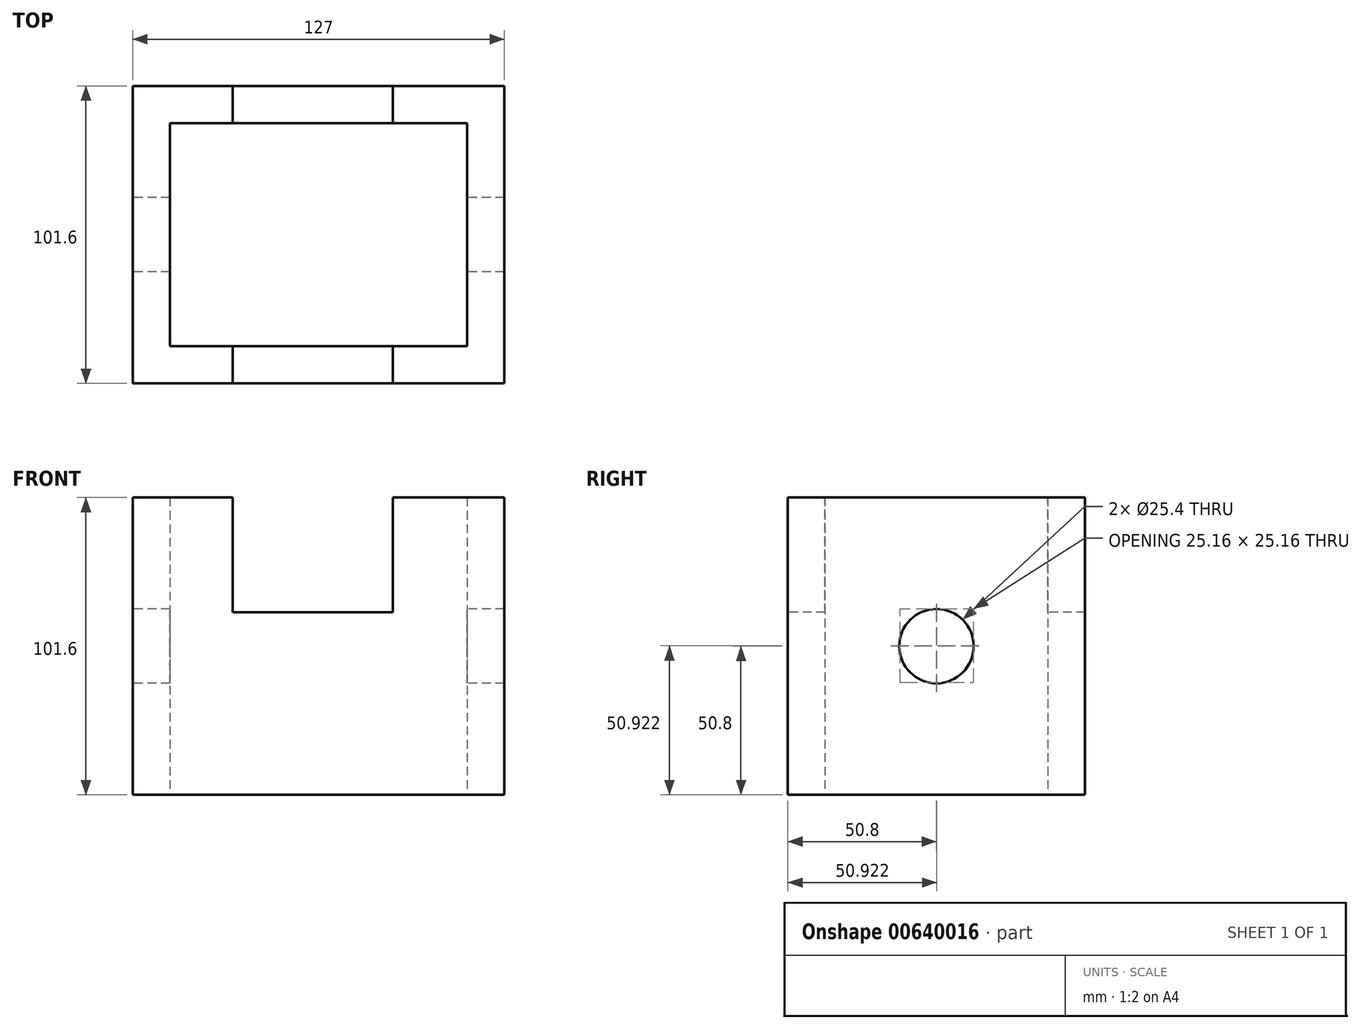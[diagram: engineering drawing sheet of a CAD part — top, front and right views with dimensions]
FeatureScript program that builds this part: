
annotation { "Feature Type Name" : "Feature", "Feature Type Description" : "" }
export const myFeature = defineFeature(function(context is Context, id is Id, definition is map)
    precondition{}
    {
        {
            var Q0;
            Q0=qCreatedBy(makeId("Top.planeOp"),FACE);
            var sketch = newSketch(context, id + "F0", { "sketchPlane" : qUnion([Q0])});
            skLineSegment(sketch, "E0.bottom", {"start": v(92.9, -48.3) * mm, "end": v(-34.1, -48.3) * mm});
            skLineSegment(sketch, "E0.top", {"start": v(92.9, 53.3) * mm, "end": v(-34.1, 53.3) * mm});
            skLineSegment(sketch, "E0.left", {"start": v(92.9, -48.3) * mm, "end": v(92.9, 53.3) * mm});
            skLineSegment(sketch, "E0.right", {"start": v(-34.1, -48.3) * mm, "end": v(-34.1, 53.3) * mm});
            skLineSegment(sketch, "E1.bottom", {"start": v(-21.4, 40.6) * mm, "end": v(80.2, 40.6) * mm});
            skLineSegment(sketch, "E1.top", {"start": v(-21.4, -35.6) * mm, "end": v(80.2, -35.6) * mm});
            skLineSegment(sketch, "E1.left", {"start": v(-21.4, 40.6) * mm, "end": v(-21.4, -35.6) * mm});
            skLineSegment(sketch, "E1.right", {"start": v(80.2, 40.6) * mm, "end": v(80.2, -35.6) * mm});
            skSolve(sketch);
        }
        {
            var Q0;
            Q0=makeQuery(id+"F0.imprint","IMPRINT",FACE,{"disambiguationData":[TD([[makeQuery(id+"F0.imprint","IMPRINT",EDGE,{"derivedFrom":sQuery(id+"F0.wireOp",EDGE,"E0.bottom")}),-1.0]])]});
            extrude(context, id + "F1", {"entities" : qUnion([Q0]), "depth" : 101.6 * mm, "offsetDistance" : 25.4 * mm});
        }
        {
            var Q0;
            Q0=makeQuery(id+"F1.opExtrude","SWEPT_FACE",FACE,{"disambiguationData":[OSD([sQuery(id+"F0.wireOp",EDGE,"E0.bottom")])]});
            var sketch = newSketch(context, id + "F2", { "sketchPlane" : qUnion([Q0])});
            skLineSegment(sketch, "E2.bottom", {"start": v(0, 101.6) * mm, "end": v(54.8, 101.6) * mm});
            skLineSegment(sketch, "E2.top", {"start": v(0, 62.4) * mm, "end": v(54.8, 62.4) * mm});
            skLineSegment(sketch, "E2.left", {"start": v(0, 101.6) * mm, "end": v(0, 62.4) * mm});
            skLineSegment(sketch, "E2.right", {"start": v(54.8, 101.6) * mm, "end": v(54.8, 62.4) * mm});
            skSolve(sketch);
        }
        {
            var Q0;
            Q0=makeQuery(id+"F2.imprint","IMPRINT",FACE,{"disambiguationData":[TD([[makeQuery(id+"F2.imprint","IMPRINT",EDGE,{"derivedFrom":sQuery(id+"F2.wireOp",EDGE,"E2.bottom")}),1.0]])]});
            extrude(context, id + "F3", {"entities" : qUnion([Q0]), "operationType" : NewBodyOperationType.REMOVE, "oppositeDirection" : true, "depth" : 152.4 * mm, "offsetDistance" : 25.4 * mm});
        }
        {
            var Q0;
            Q0=makeQuery(id+"F1.opExtrude","SWEPT_FACE",FACE,{"disambiguationData":[OSD([sQuery(id+"F0.wireOp",EDGE,"E0.right")])]});
            var sketch = newSketch(context, id + "F4", { "sketchPlane" : qUnion([Q0])});
            skPoint(sketch, "E3.centerSnap0", {"position": v(-53.3, 50.8) * mm});
            skPoint(sketch, "E3.centerSnap1", {"position": v(-2.5, 101.6) * mm});
            skCircle(sketch, "E4", {"center": v(-2.5, 50.8) * mm, "radius": 12.7 * mm});
            skSolve(sketch);
        }
        {
            var Q0;
            Q0=makeQuery(id+"F4.imprint","IMPRINT",FACE,{"disambiguationData":[TD([[makeQuery(id+"F4.imprint","IMPRINT",EDGE,{"derivedFrom":sQuery(id+"F4.wireOp",EDGE,"E4")}),1.0]])]});
            extrude(context, id + "F5", {"entities" : qUnion([Q0]), "operationType" : NewBodyOperationType.REMOVE, "oppositeDirection" : true, "depth" : 203.2 * mm, "offsetDistance" : 25.4 * mm});
        }
    });
